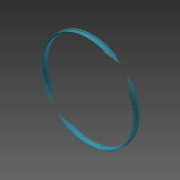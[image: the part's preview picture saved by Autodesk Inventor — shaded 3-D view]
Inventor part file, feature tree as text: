
AUTODESK INVENTOR PART (.ipt)
format: ipt  version: 2015 (Build 190159000, 159)  size: 1,155,072 bytes
history: native  units: mm
features: other x7, hole x4, sketch x4, pattern_circular x3
ambient origin geometry x8: Origin, YZ Plane, XZ Plane, XY Plane, X Axis, Y Axis, Z Axis, Center Point
bodies: Body1 (feature_tree)
feature tree (18):
  other  "Bryła1"
  other  "Obręcz"
  other  "Płaszczyzna do otworu na nypel 1"
  hole  "Otwór na nypel 1"  [1 undecoded]
  pattern_circular  "Szyk otworów na nypel 1"  [2 undecoded]
  other  "Płaszczyzna do otworu na nypel 2"
  other  "Płaszczyzna do otworu na nypel 2.2"
  hole  "Otwór na nypel 2"  [1 undecoded]
  pattern_circular  "Szyk otworów na nypel 2"  [2 undecoded]
  other  "Płaszczyzna do otworu na wentyl"
  hole  "Otwór na wentyl"  [1 undecoded]
  other  "Płaszczyzna konstrukcyjna5"
  hole  "Otwór7"  [1 undecoded]
  pattern_circular  "Szyk kołowy5"  [2 undecoded]
  sketch  "Szkic1"
  sketch  "Szkic4"
  sketch  "Szkic6"
  sketch  "Szkic7"
note: 10 required parameter values undecoded (feature->parameter linkage not recoverable at this tier; creation-order binding heuristic only, values carry confidence <= 0.55)
